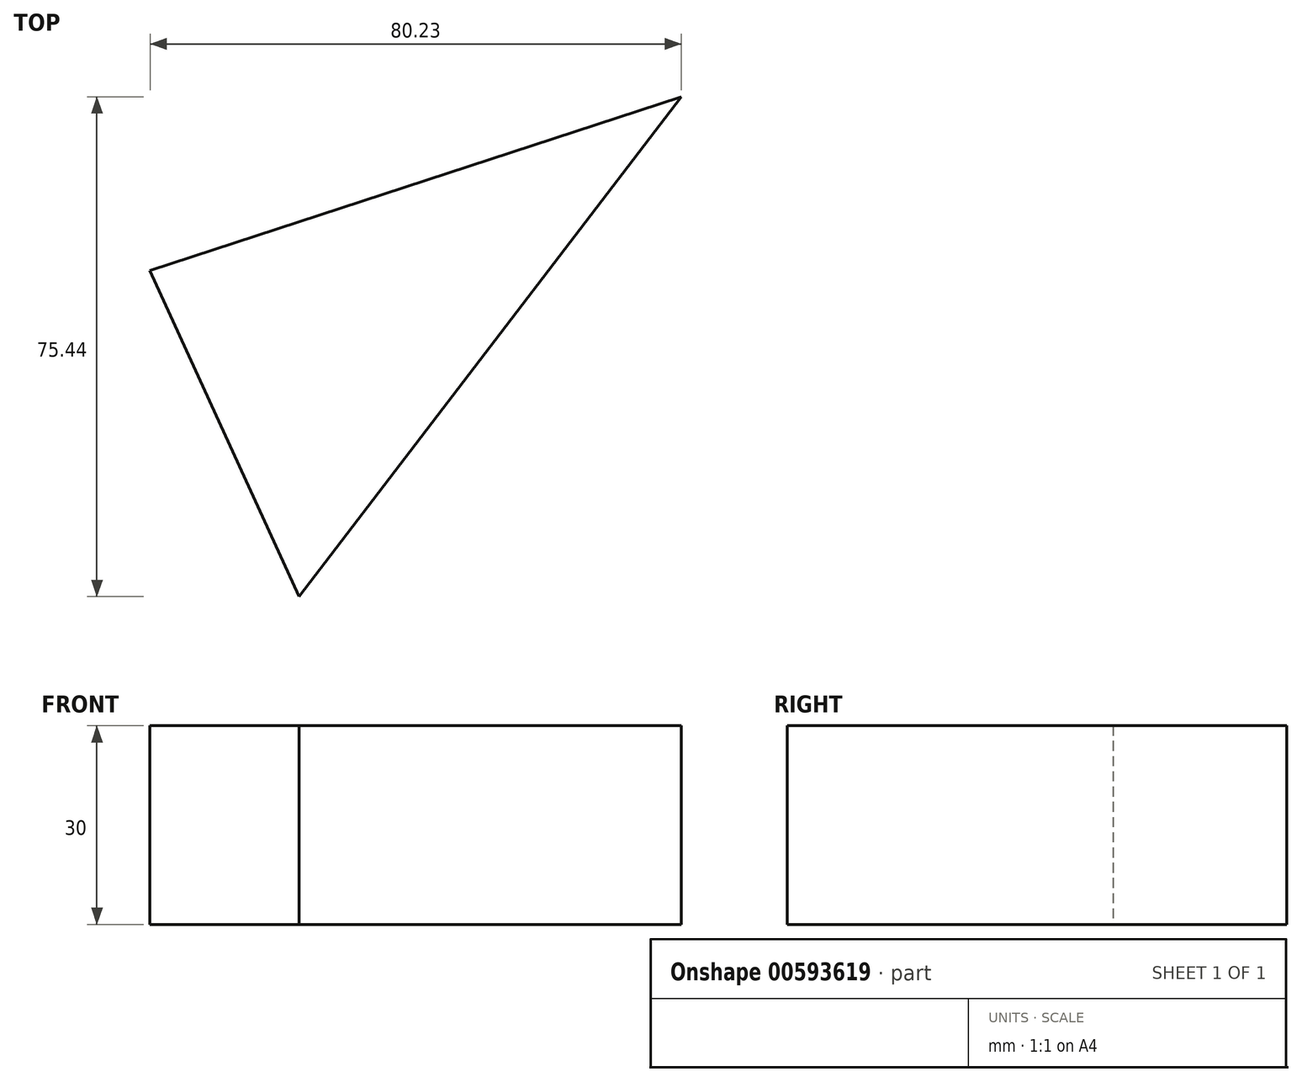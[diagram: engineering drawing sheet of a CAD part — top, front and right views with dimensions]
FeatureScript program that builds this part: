
annotation { "Feature Type Name" : "Feature", "Feature Type Description" : "" }
export const myFeature = defineFeature(function(context is Context, id is Id, definition is map)
    precondition{}
    {
        {
            var Q0;
            Q0=qCreatedBy(makeId("Top.planeOp"),FACE);
            var sketch = newSketch(context, id + "F0", { "sketchPlane" : qUnion([Q0])});
            skLineSegment(sketch, "E0", {"start": v(-39, 12.9) * mm, "end": v(41.24, 39.14) * mm});
            skLineSegment(sketch, "E1", {"start": v(41.24, 39.14) * mm, "end": v(-16.5, -36.3) * mm});
            skLineSegment(sketch, "E2", {"start": v(-16.5, -36.3) * mm, "end": v(-39, 12.9) * mm});
            skSolve(sketch);
        }
        {
            var Q0;
            Q0 = qSketchRegion(id + "F0", true);
            extrude(context, id + "F1", {"entities" : qUnion([Q0]), "depth" : 30 * mm, "offsetDistance" : 25.4 * mm});
        }
        {
            var Q0;
            Q0=qCreatedBy(makeId("Front.planeOp"),FACE);
            var sketch = newSketch(context, id + "F2", { "sketchPlane" : qUnion([Q0])});
            skLineSegment(sketch, "E3.bottom", {"start": v(-62.1, 32.03) * mm, "end": v(-118.67, 32.03) * mm});
            skLineSegment(sketch, "E3.top", {"start": v(-62.1, -38.38) * mm, "end": v(-118.67, -38.38) * mm});
            skLineSegment(sketch, "E3.left", {"start": v(-62.1, 32.03) * mm, "end": v(-62.1, -38.38) * mm});
            skLineSegment(sketch, "E3.right", {"start": v(-118.67, 32.03) * mm, "end": v(-118.67, -38.38) * mm});
            skSolve(sketch);
        }
        {
            var Q0;
            Q0=makeQuery(id+"F2.imprint","IMPRINT",FACE,{"disambiguationData":[TD([[makeQuery(id+"F2.imprint","IMPRINT",EDGE,{"derivedFrom":sQuery(id+"F2.wireOp",EDGE,"E3.bottom")}),1.0]])]});
            var Q1;
            Q1=sQuery(id+"F2.wireOp",EDGE,"E3.bottom");
            extrude(context, id + "F3", {"entities" : qUnion([Q0]), "bodyType" : ToolBodyType.SURFACE, "surfaceEntities" : qUnion([Q1]), "depth" : 44.92 * mm, "offsetDistance" : 25.4 * mm});
        }
    });
